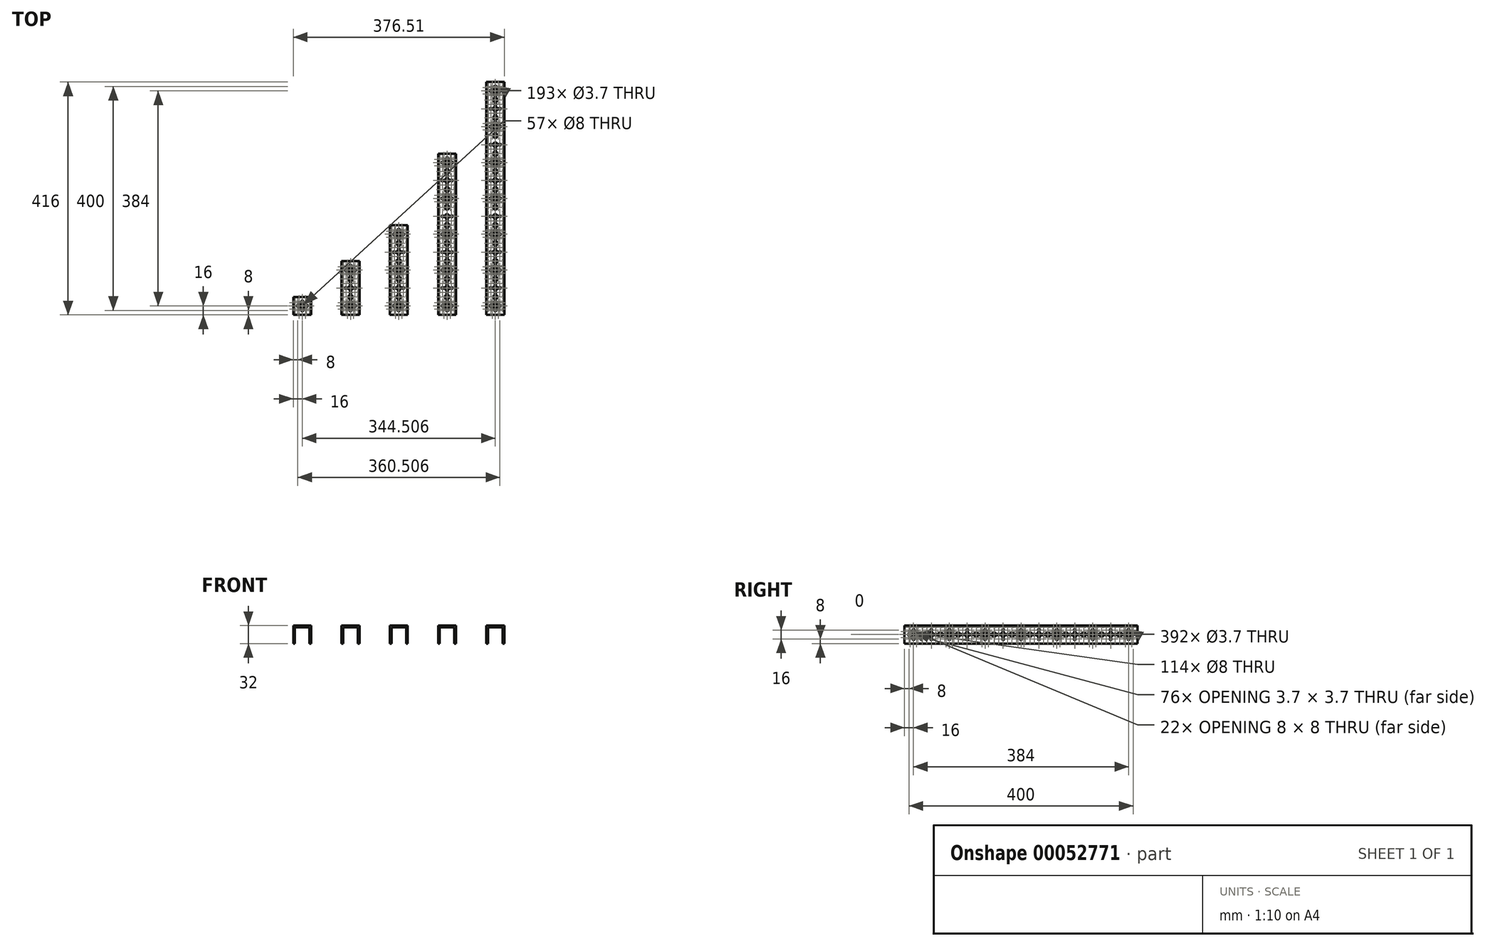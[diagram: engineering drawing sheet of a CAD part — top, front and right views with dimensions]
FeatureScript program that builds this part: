
annotation { "Feature Type Name" : "Feature", "Feature Type Description" : "" }
export const myFeature = defineFeature(function(context is Context, id is Id, definition is map)
    precondition{}
    {
        {
            var Q0;
            Q0=qCreatedBy(makeId("Front.planeOp"),FACE);
            var sketch = newSketch(context, id + "F0", { "sketchPlane" : qUnion([Q0])});
            skLineSegment(sketch, "E0", {"start": v(-16, 0) * mm, "end": v(16, 0) * mm});
            skLineSegment(sketch, "E1", {"start": v(16, 0) * mm, "end": v(16, -32) * mm});
            skLineSegment(sketch, "E2", {"start": v(-16, 0) * mm, "end": v(-16, -32) * mm});
            skLineSegment(sketch, "E3.0", {"start": v(-13, -3) * mm, "end": v(-13, -32) * mm});
            skLineSegment(sketch, "E3.1", {"start": v(-13, -3) * mm, "end": v(13, -3) * mm});
            skLineSegment(sketch, "E3.2", {"start": v(13, -3) * mm, "end": v(13, -32) * mm});
            skLineSegment(sketch, "E4", {"start": v(-16, -32) * mm, "end": v(-13, -32) * mm});
            skLineSegment(sketch, "E5", {"start": v(13, -32) * mm, "end": v(16, -32) * mm});
            skSolve(sketch);
        }
        {
            var Q0;
            Q0 = qSketchRegion(id + "F0", true);
            extrude(context, id + "F1", {"entities" : qUnion([Q0]), "oppositeDirection" : true, "depth" : 32 * mm});
        }
        {
            var Q0;
            Q0=makeQuery(id+"F1.opExtrude","SWEPT_FACE",FACE,{"disambiguationData":[OSD([sQuery(id+"F0.wireOp",EDGE,"E1")])]});
            var sketch = newSketch(context, id + "F2", { "sketchPlane" : qUnion([Q0])});
            skCircle(sketch, "E6", {"center": v(16, -16) * mm, "radius": 4 * mm});
            skCircle(sketch, "E7", {"center": v(10.34, -10.34) * mm, "radius": 1.85 * mm});
            skCircle(sketch, "E8", {"center": v(16, -8) * mm, "radius": 1.85 * mm});
            skCircle(sketch, "E9", {"center": v(21.66, -10.34) * mm, "radius": 1.85 * mm});
            skCircle(sketch, "E10", {"center": v(24, -16) * mm, "radius": 1.85 * mm});
            skCircle(sketch, "E11", {"center": v(21.66, -21.66) * mm, "radius": 1.85 * mm});
            skCircle(sketch, "E12", {"center": v(16, -24) * mm, "radius": 1.85 * mm});
            skCircle(sketch, "E13", {"center": v(8, -16) * mm, "radius": 1.85 * mm});
            skCircle(sketch, "E14", {"center": v(10.34, -21.66) * mm, "radius": 1.85 * mm});
            skCircle(sketch, "E15", {"center": v(16, -16) * mm, "radius": 8 * mm});
            skLineSegment(sketch, "E16", {"start": v(16, -8) * mm, "end": v(16, -24) * mm});
            skLineSegment(sketch, "E17", {"start": v(8, -16) * mm, "end": v(24, -16) * mm});
            skLineSegment(sketch, "E18", {"start": v(21.66, -10.34) * mm, "end": v(10.34, -21.66) * mm});
            skLineSegment(sketch, "E19", {"start": v(10.34, -10.34) * mm, "end": v(21.66, -21.66) * mm});
            skSolve(sketch);
        }
        {
            var Q0;
            Q0=makeQuery(id+"F1.opExtrude","SWEPT_FACE",FACE,{"disambiguationData":[OSD([sQuery(id+"F0.wireOp",EDGE,"E0")])]});
            var sketch = newSketch(context, id + "F3", { "sketchPlane" : qUnion([Q0])});
            skCircle(sketch, "E20", {"center": v(0, 16) * mm, "radius": 4 * mm});
            skCircle(sketch, "E21", {"center": v(-5.66, 21.66) * mm, "radius": 1.85 * mm});
            skCircle(sketch, "E22", {"center": v(0, 24) * mm, "radius": 1.85 * mm});
            skCircle(sketch, "E23", {"center": v(5.66, 21.66) * mm, "radius": 1.85 * mm});
            skCircle(sketch, "E24", {"center": v(8, 16) * mm, "radius": 1.85 * mm});
            skCircle(sketch, "E25", {"center": v(5.66, 10.34) * mm, "radius": 1.85 * mm});
            skCircle(sketch, "E26", {"center": v(0, 8) * mm, "radius": 1.85 * mm});
            skCircle(sketch, "E27", {"center": v(-8, 16) * mm, "radius": 1.85 * mm});
            skCircle(sketch, "E28", {"center": v(-5.66, 10.34) * mm, "radius": 1.85 * mm});
            skCircle(sketch, "E29", {"center": v(0, 16) * mm, "radius": 8 * mm});
            skLineSegment(sketch, "E30", {"start": v(0, 24) * mm, "end": v(0, 8) * mm});
            skLineSegment(sketch, "E31", {"start": v(-8, 16) * mm, "end": v(8, 16) * mm});
            skLineSegment(sketch, "E32", {"start": v(5.66, 21.66) * mm, "end": v(-5.66, 10.34) * mm});
            skLineSegment(sketch, "E33", {"start": v(-5.66, 21.66) * mm, "end": v(5.66, 10.34) * mm});
            skSolve(sketch);
        }
        {
            var Q0;
            Q0=sQuery(id+"F3.wireOp",VERTEX,"E21.center");
            var Q1;
            Q1=sQuery(id+"F3.wireOp",VERTEX,"E22.center");
            var Q2;
            Q2=sQuery(id+"F3.wireOp",VERTEX,"E23.center");
            var Q3;
            Q3=sQuery(id+"F3.wireOp",VERTEX,"E31.start");
            var Q4;
            Q4=sQuery(id+"F3.wireOp",VERTEX,"E24.center");
            var Q5;
            Q5=sQuery(id+"F3.wireOp",VERTEX,"E28.center");
            var Q6;
            Q6=sQuery(id+"F3.wireOp",VERTEX,"E30.end");
            var Q7;
            Q7=sQuery(id+"F3.wireOp",VERTEX,"E33.end");
            var Q8;
            Q8=sQuery(id+"F2.wireOp",VERTEX,"E16.start");
            var Q9;
            Q9=sQuery(id+"F2.wireOp",VERTEX,"E9.center");
            var Q10;
            Q10=sQuery(id+"F2.wireOp",VERTEX,"E10.center");
            var Q11;
            Q11=sQuery(id+"F2.wireOp",VERTEX,"E7.center");
            var Q12;
            Q12=sQuery(id+"F2.wireOp",VERTEX,"E17.start");
            var Q13;
            Q13=sQuery(id+"F2.wireOp",VERTEX,"E14.center");
            var Q14;
            Q14=sQuery(id+"F2.wireOp",VERTEX,"E16.end");
            var Q15;
            Q15=sQuery(id+"F2.wireOp",VERTEX,"E19.end");
            var Q16;
            Q16=makeQuery(id+"F1.opExtrude","SWEPT_BODY",BODY,{"disambiguationData":[OSD([sQuery(id+"F0.wireOp",EDGE,"E0"),sQuery(id+"F0.wireOp",EDGE,"E1"),sQuery(id+"F0.wireOp",EDGE,"E2"),sQuery(id+"F0.wireOp",EDGE,"E3.0"),sQuery(id+"F0.wireOp",EDGE,"E3.1"),sQuery(id+"F0.wireOp",EDGE,"E3.2"),sQuery(id+"F0.wireOp",EDGE,"E4"),sQuery(id+"F0.wireOp",EDGE,"E5")])]});
            hole(context, id + "F4", {"style" : HoleStyle.SIMPLE, "holeDiameter" : 3.7 * mm, "endStyle" : HoleEndStyle.THROUGH, "locations" : qUnion([Q0, Q1, Q2, Q3, Q4, Q5, Q6, Q7, Q8, Q9, Q10, Q11, Q12, Q13, Q14, Q15]), "scope" : qUnion([Q16])});
        }
        {
            var Q0;
            Q0=sQuery(id+"F3.wireOp",VERTEX,"E29.center");
            var Q1;
            Q1=sQuery(id+"F2.wireOp",VERTEX,"E6.center");
            var Q2;
            Q2=makeQuery(id+"F1.opExtrude","SWEPT_BODY",BODY,{"disambiguationData":[OSD([sQuery(id+"F0.wireOp",EDGE,"E0"),sQuery(id+"F0.wireOp",EDGE,"E1"),sQuery(id+"F0.wireOp",EDGE,"E2"),sQuery(id+"F0.wireOp",EDGE,"E3.0"),sQuery(id+"F0.wireOp",EDGE,"E3.1"),sQuery(id+"F0.wireOp",EDGE,"E3.2"),sQuery(id+"F0.wireOp",EDGE,"E4"),sQuery(id+"F0.wireOp",EDGE,"E5")])]});
            hole(context, id + "F5", {"style" : HoleStyle.SIMPLE, "holeDiameter" : 8 * mm, "endStyle" : HoleEndStyle.THROUGH, "locations" : qUnion([Q0, Q1]), "scope" : qUnion([Q2])});
        }
        {
            var Q0;
            Q0=makeQuery(id+"F1.opExtrude","SWEPT_BODY",BODY,{"disambiguationData":[OSD([sQuery(id+"F0.wireOp",EDGE,"E0"),sQuery(id+"F0.wireOp",EDGE,"E1"),sQuery(id+"F0.wireOp",EDGE,"E2"),sQuery(id+"F0.wireOp",EDGE,"E3.0"),sQuery(id+"F0.wireOp",EDGE,"E3.1"),sQuery(id+"F0.wireOp",EDGE,"E3.2"),sQuery(id+"F0.wireOp",EDGE,"E4"),sQuery(id+"F0.wireOp",EDGE,"E5")])]});
            transform(context, id + "F6", {"entities" : qUnion([Q0]), "transformType" : TransformType.TRANSLATION_3D, "dx" : 86.13 * mm, "dy" : 0 * mm, "dz" : 0 * mm, "makeCopy" : true});
        }
        {
            var Q0;
            Q0=makeQuery(id+"F6.opPattern","COPY",FACE,{"derivedFrom":makeQuery(id+"F1.opExtrude","CAP_FACE",FACE,{"disambiguationData":[OSD([sQuery(id+"F0.wireOp",EDGE,"E0"),sQuery(id+"F0.wireOp",EDGE,"E1"),sQuery(id+"F0.wireOp",EDGE,"E2"),sQuery(id+"F0.wireOp",EDGE,"E3.0"),sQuery(id+"F0.wireOp",EDGE,"E3.1"),sQuery(id+"F0.wireOp",EDGE,"E3.2"),sQuery(id+"F0.wireOp",EDGE,"E4"),sQuery(id+"F0.wireOp",EDGE,"E5")])],"isStart":false}),"instanceName":"1"});
            extrude(context, id + "F7", {"entities" : qUnion([Q0]), "operationType" : NewBodyOperationType.ADD, "depth" : 64 * mm});
        }
        {
            var Q0;
            {var subQ0=sQuery(id+"F0.wireOp",EDGE,"E1");Q0=makeQuery(id+"F7.boolean.opBoolean","MERGE",FACE,{"derivedFrom":[makeQuery(id+"F6.opPattern","COPY",FACE,{"derivedFrom":makeQuery(id+"F1.opExtrude","SWEPT_FACE",FACE,{"disambiguationData":[OSD([subQ0])]}),"instanceName":"1"}),makeQuery(id+"F7.opExtrude","SWEPT_FACE",FACE,{"disambiguationData":[OSD([subQ0])]})]});}
            var sketch = newSketch(context, id + "F8", { "sketchPlane" : qUnion([Q0])});
            skCircle(sketch, "E34", {"center": v(48, -24) * mm, "radius": 1.85 * mm});
            skLineSegment(sketch, "E35", {"start": v(48, -8) * mm, "end": v(48, -24) * mm});
            skLineSegment(sketch, "E36", {"start": v(40, -16) * mm, "end": v(56, -16) * mm});
            skCircle(sketch, "E37", {"center": v(48, -16) * mm, "radius": 8 * mm});
            skCircle(sketch, "E38", {"center": v(48, -16) * mm, "radius": 4 * mm});
            skCircle(sketch, "E39", {"center": v(48, -8) * mm, "radius": 1.85 * mm});
            skCircle(sketch, "E40", {"center": v(56, -16) * mm, "radius": 1.85 * mm});
            skCircle(sketch, "E41", {"center": v(40, -16) * mm, "radius": 1.85 * mm});
            skCircle(sketch, "E42.0", {"center": v(24, -16) * mm, "radius": 1.85 * mm});
            skCircle(sketch, "E43", {"center": v(80, -24) * mm, "radius": 1.85 * mm});
            skLineSegment(sketch, "E44", {"start": v(85.66, -10.34) * mm, "end": v(74.34, -21.66) * mm});
            skLineSegment(sketch, "E45", {"start": v(74.34, -10.34) * mm, "end": v(85.66, -21.66) * mm});
            skLineSegment(sketch, "E46", {"start": v(80, -8) * mm, "end": v(80, -24) * mm});
            skLineSegment(sketch, "E47", {"start": v(72, -16) * mm, "end": v(88, -16) * mm});
            skCircle(sketch, "E48", {"center": v(80, -16) * mm, "radius": 8 * mm});
            skCircle(sketch, "E49", {"center": v(74.34, -21.66) * mm, "radius": 1.85 * mm});
            skCircle(sketch, "E50", {"center": v(80, -16) * mm, "radius": 4 * mm});
            skCircle(sketch, "E51", {"center": v(74.34, -10.34) * mm, "radius": 1.85 * mm});
            skCircle(sketch, "E52", {"center": v(80, -8) * mm, "radius": 1.85 * mm});
            skCircle(sketch, "E53", {"center": v(85.66, -10.34) * mm, "radius": 1.85 * mm});
            skCircle(sketch, "E54", {"center": v(88, -16) * mm, "radius": 1.85 * mm});
            skCircle(sketch, "E55", {"center": v(85.66, -21.66) * mm, "radius": 1.85 * mm});
            skCircle(sketch, "E56", {"center": v(72, -16) * mm, "radius": 1.85 * mm});
            skCircle(sketch, "E57", {"center": v(32, -16) * mm, "radius": 4 * mm});
            skCircle(sketch, "E58", {"center": v(64, -16) * mm, "radius": 4 * mm});
            skSolve(sketch);
        }
        {
            var Q0;
            {var subQ0=sQuery(id+"F0.wireOp",EDGE,"E0");Q0=makeQuery(id+"F7.boolean.opBoolean","MERGE",FACE,{"derivedFrom":[makeQuery(id+"F6.opPattern","COPY",FACE,{"derivedFrom":makeQuery(id+"F1.opExtrude","SWEPT_FACE",FACE,{"disambiguationData":[OSD([subQ0])]}),"instanceName":"1"}),makeQuery(id+"F7.opExtrude","SWEPT_FACE",FACE,{"disambiguationData":[OSD([subQ0])]})]});}
            var sketch = newSketch(context, id + "F9", { "sketchPlane" : qUnion([Q0])});
            skCircle(sketch, "E59", {"center": v(86.13, 32) * mm, "radius": 4 * mm});
            skCircle(sketch, "E60.0", {"center": v(86.13, 24) * mm, "radius": 1.85 * mm});
            skCircle(sketch, "E61", {"center": v(86.13, 48) * mm, "radius": 4 * mm});
            skCircle(sketch, "E62", {"center": v(86.13, 40) * mm, "radius": 1.85 * mm});
            skLineSegment(sketch, "E63", {"start": v(86.13, 40) * mm, "end": v(86.13, 48) * mm});
            skCircle(sketch, "E64.1.0", {"center": v(78.13, 48) * mm, "radius": 1.85 * mm});
            skCircle(sketch, "E64.2.0", {"center": v(86.13, 56) * mm, "radius": 1.85 * mm});
            skCircle(sketch, "E64.3.0", {"center": v(94.13, 48) * mm, "radius": 1.85 * mm});
            skLineSegment(sketch, "E64.anchor1", {"start": v(86.13, 48) * mm, "end": v(86.13, 40) * mm, "construction": true});
            skLineSegment(sketch, "E64.anchor2", {"start": v(86.13, 48) * mm, "end": v(94.13, 48) * mm, "construction": true});
            skCircle(sketch, "E65", {"center": v(86.13, 64) * mm, "radius": 4 * mm});
            skCircle(sketch, "E66", {"center": v(86.13, 80) * mm, "radius": 4 * mm});
            skCircle(sketch, "E67", {"center": v(86.13, 72) * mm, "radius": 1.85 * mm});
            skLineSegment(sketch, "E68", {"start": v(86.13, 80) * mm, "end": v(86.13, 72) * mm});
            skCircle(sketch, "E69.1.0", {"center": v(91.78, 74.34) * mm, "radius": 1.85 * mm});
            skCircle(sketch, "E69.2.0", {"center": v(94.13, 80) * mm, "radius": 1.85 * mm});
            skCircle(sketch, "E69.3.0", {"center": v(91.78, 85.66) * mm, "radius": 1.85 * mm});
            skCircle(sketch, "E69.4.0", {"center": v(86.13, 88) * mm, "radius": 1.85 * mm});
            skCircle(sketch, "E69.5.0", {"center": v(80.47, 85.66) * mm, "radius": 1.85 * mm});
            skCircle(sketch, "E69.6.0", {"center": v(78.13, 80) * mm, "radius": 1.85 * mm});
            skCircle(sketch, "E69.7.0", {"center": v(80.47, 74.34) * mm, "radius": 1.85 * mm});
            skSolve(sketch);
        }
        {
            var Q0;
            Q0=sQuery(id+"F8.wireOp",VERTEX,"E39.center");
            var Q1;
            Q1=sQuery(id+"F8.wireOp",VERTEX,"E41.center");
            var Q2;
            Q2=sQuery(id+"F8.wireOp",VERTEX,"E40.center");
            var Q3;
            Q3=sQuery(id+"F8.wireOp",VERTEX,"E34.center");
            var Q4;
            Q4=sQuery(id+"F8.wireOp",VERTEX,"E51.center");
            var Q5;
            Q5=sQuery(id+"F8.wireOp",VERTEX,"E47.start");
            var Q6;
            Q6=sQuery(id+"F8.wireOp",VERTEX,"E44.end");
            var Q7;
            Q7=sQuery(id+"F8.wireOp",VERTEX,"E46.end");
            var Q8;
            Q8=sQuery(id+"F8.wireOp",VERTEX,"E47.end");
            var Q9;
            Q9=sQuery(id+"F8.wireOp",VERTEX,"E44.start");
            var Q10;
            Q10=sQuery(id+"F8.wireOp",VERTEX,"E52.center");
            var Q11;
            Q11=sQuery(id+"F8.wireOp",VERTEX,"E45.end");
            var Q12;
            Q12=sQuery(id+"F9.wireOp",VERTEX,"E64.3.0.center");
            var Q13;
            Q13=sQuery(id+"F9.wireOp",VERTEX,"E64.anchor1.end");
            var Q14;
            Q14=sQuery(id+"F9.wireOp",VERTEX,"E64.1.0.center");
            var Q15;
            Q15=sQuery(id+"F9.wireOp",VERTEX,"E64.2.0.center");
            var Q16;
            Q16=sQuery(id+"F9.wireOp",VERTEX,"E69.1.0.center");
            var Q17;
            Q17=sQuery(id+"F9.wireOp",VERTEX,"E68.end");
            var Q18;
            Q18=sQuery(id+"F9.wireOp",VERTEX,"E69.7.0.center");
            var Q19;
            Q19=sQuery(id+"F9.wireOp",VERTEX,"E69.6.0.center");
            var Q20;
            Q20=sQuery(id+"F9.wireOp",VERTEX,"E69.6.0.center");
            var Q21;
            Q21=sQuery(id+"F9.wireOp",VERTEX,"E69.5.0.center");
            var Q22;
            Q22=sQuery(id+"F9.wireOp",VERTEX,"E69.4.0.center");
            var Q23;
            Q23=sQuery(id+"F9.wireOp",VERTEX,"E69.3.0.center");
            var Q24;
            Q24=sQuery(id+"F9.wireOp",VERTEX,"E69.2.0.center");
            var Q25;
            Q25=makeQuery(id+"F6.opPattern","COPY",BODY,{"derivedFrom":makeQuery(id+"F1.opExtrude","SWEPT_BODY",BODY,{"disambiguationData":[OSD([sQuery(id+"F0.wireOp",EDGE,"E0"),sQuery(id+"F0.wireOp",EDGE,"E1"),sQuery(id+"F0.wireOp",EDGE,"E2"),sQuery(id+"F0.wireOp",EDGE,"E3.0"),sQuery(id+"F0.wireOp",EDGE,"E3.1"),sQuery(id+"F0.wireOp",EDGE,"E3.2"),sQuery(id+"F0.wireOp",EDGE,"E4"),sQuery(id+"F0.wireOp",EDGE,"E5")])]}),"instanceName":"1"});
            hole(context, id + "F10", {"style" : HoleStyle.SIMPLE, "holeDiameter" : 3.7 * mm, "endStyle" : HoleEndStyle.THROUGH, "locations" : qUnion([Q0, Q1, Q2, Q3, Q4, Q5, Q6, Q7, Q8, Q9, Q10, Q11, Q12, Q13, Q14, Q15, Q16, Q17, Q18, Q19, Q20, Q21, Q22, Q23, Q24]), "scope" : qUnion([Q25])});
        }
        {
            var Q0;
            Q0=sQuery(id+"F8.wireOp",VERTEX,"E37.center");
            var Q1;
            Q1=sQuery(id+"F8.wireOp",VERTEX,"E57.center");
            var Q2;
            Q2=sQuery(id+"F8.wireOp",VERTEX,"E58.center");
            var Q3;
            Q3=sQuery(id+"F8.wireOp",VERTEX,"E48.center");
            var Q4;
            Q4=sQuery(id+"F9.wireOp",VERTEX,"E59.center");
            var Q5;
            Q5=sQuery(id+"F9.wireOp",VERTEX,"E61.center");
            var Q6;
            Q6=sQuery(id+"F9.wireOp",VERTEX,"E65.center");
            var Q7;
            Q7=sQuery(id+"F9.wireOp",VERTEX,"E66.center");
            var Q8;
            Q8=makeQuery(id+"F6.opPattern","COPY",BODY,{"derivedFrom":makeQuery(id+"F1.opExtrude","SWEPT_BODY",BODY,{"disambiguationData":[OSD([sQuery(id+"F0.wireOp",EDGE,"E0"),sQuery(id+"F0.wireOp",EDGE,"E1"),sQuery(id+"F0.wireOp",EDGE,"E2"),sQuery(id+"F0.wireOp",EDGE,"E3.0"),sQuery(id+"F0.wireOp",EDGE,"E3.1"),sQuery(id+"F0.wireOp",EDGE,"E3.2"),sQuery(id+"F0.wireOp",EDGE,"E4"),sQuery(id+"F0.wireOp",EDGE,"E5")])]}),"instanceName":"1"});
            hole(context, id + "F11", {"style" : HoleStyle.SIMPLE, "holeDiameter" : 8 * mm, "endStyle" : HoleEndStyle.THROUGH, "locations" : qUnion([Q0, Q1, Q2, Q3, Q4, Q5, Q6, Q7]), "scope" : qUnion([Q8])});
        }
        {
            var Q0;
            Q0=makeQuery(id+"F6.opPattern","COPY",BODY,{"derivedFrom":makeQuery(id+"F1.opExtrude","SWEPT_BODY",BODY,{"disambiguationData":[OSD([sQuery(id+"F0.wireOp",EDGE,"E0"),sQuery(id+"F0.wireOp",EDGE,"E1"),sQuery(id+"F0.wireOp",EDGE,"E2"),sQuery(id+"F0.wireOp",EDGE,"E3.0"),sQuery(id+"F0.wireOp",EDGE,"E3.1"),sQuery(id+"F0.wireOp",EDGE,"E3.2"),sQuery(id+"F0.wireOp",EDGE,"E4"),sQuery(id+"F0.wireOp",EDGE,"E5")])]}),"instanceName":"1"});
            transform(context, id + "F12", {"entities" : qUnion([Q0]), "transformType" : TransformType.TRANSLATION_3D, "dx" : 86.13 * mm, "dy" : 0 * mm, "dz" : 0 * mm, "makeCopy" : true});
        }
        {
            var Q0;
            Q0=makeQuery(id+"F12.opPattern","COPY",FACE,{"derivedFrom":makeQuery(id+"F7.opExtrude","CAP_FACE",FACE,{"disambiguationData":[OSD([sQuery(id+"F0.wireOp",EDGE,"E0"),sQuery(id+"F0.wireOp",EDGE,"E1"),sQuery(id+"F0.wireOp",EDGE,"E2"),sQuery(id+"F0.wireOp",EDGE,"E3.0"),sQuery(id+"F0.wireOp",EDGE,"E3.1"),sQuery(id+"F0.wireOp",EDGE,"E3.2"),sQuery(id+"F0.wireOp",EDGE,"E4"),sQuery(id+"F0.wireOp",EDGE,"E5")])],"isStart":false}),"instanceName":"1"});
            extrude(context, id + "F13", {"entities" : qUnion([Q0]), "operationType" : NewBodyOperationType.ADD, "depth" : 64 * mm});
        }
        {
            var Q0;
            {var subQ0=sQuery(id+"F0.wireOp",EDGE,"E1");Q0=makeQuery(id+"F13.boolean.opBoolean","MERGE",FACE,{"derivedFrom":[makeQuery(id+"F12.opPattern","COPY",FACE,{"derivedFrom":makeQuery(id+"F7.boolean.opBoolean","MERGE",FACE,{"derivedFrom":[makeQuery(id+"F6.opPattern","COPY",FACE,{"derivedFrom":makeQuery(id+"F1.opExtrude","SWEPT_FACE",FACE,{"disambiguationData":[OSD([subQ0])]}),"instanceName":"1"}),makeQuery(id+"F7.opExtrude","SWEPT_FACE",FACE,{"disambiguationData":[OSD([subQ0])]})]}),"instanceName":"1"}),makeQuery(id+"F13.opExtrude","SWEPT_FACE",FACE,{"disambiguationData":[OSD([subQ0])]})]});}
            var sketch = newSketch(context, id + "F14", { "sketchPlane" : qUnion([Q0])});
            skCircle(sketch, "E70", {"center": v(112, -16) * mm, "radius": 8 * mm});
            skCircle(sketch, "E71", {"center": v(128, -16) * mm, "radius": 4 * mm});
            skCircle(sketch, "E72", {"center": v(96, -16) * mm, "radius": 4 * mm});
            skCircle(sketch, "E73.0", {"center": v(88, -16) * mm, "radius": 1.85 * mm});
            skCircle(sketch, "E74", {"center": v(138.34, -10.34) * mm, "radius": 1.85 * mm});
            skCircle(sketch, "E75", {"center": v(144, -16) * mm, "radius": 4 * mm});
            skCircle(sketch, "E76", {"center": v(149.66, -10.34) * mm, "radius": 1.85 * mm});
            skCircle(sketch, "E77", {"center": v(144, -8) * mm, "radius": 1.85 * mm});
            skCircle(sketch, "E78", {"center": v(149.66, -21.66) * mm, "radius": 1.85 * mm});
            skCircle(sketch, "E79", {"center": v(152, -16) * mm, "radius": 1.85 * mm});
            skCircle(sketch, "E80", {"center": v(138.34, -21.66) * mm, "radius": 1.85 * mm});
            skCircle(sketch, "E81", {"center": v(144, -16) * mm, "radius": 8 * mm});
            skCircle(sketch, "E82", {"center": v(112, -24) * mm, "radius": 1.85 * mm});
            skLineSegment(sketch, "E83", {"start": v(104, -16) * mm, "end": v(120, -16) * mm});
            skLineSegment(sketch, "E84", {"start": v(112, -8) * mm, "end": v(112, -24) * mm});
            skCircle(sketch, "E85", {"center": v(112, -16) * mm, "radius": 4 * mm});
            skLineSegment(sketch, "E86", {"start": v(136, -16) * mm, "end": v(152, -16) * mm});
            skLineSegment(sketch, "E87", {"start": v(144, -8) * mm, "end": v(144, -24) * mm});
            skLineSegment(sketch, "E88", {"start": v(138.34, -10.34) * mm, "end": v(149.66, -21.66) * mm});
            skCircle(sketch, "E89", {"center": v(120, -16) * mm, "radius": 1.85 * mm});
            skCircle(sketch, "E90", {"center": v(112, -8) * mm, "radius": 1.85 * mm});
            skCircle(sketch, "E91", {"center": v(104, -16) * mm, "radius": 1.85 * mm});
            skLineSegment(sketch, "E92", {"start": v(149.66, -10.34) * mm, "end": v(138.34, -21.66) * mm});
            skCircle(sketch, "E93", {"center": v(144, -24) * mm, "radius": 1.85 * mm});
            skCircle(sketch, "E94", {"center": v(136, -16) * mm, "radius": 1.85 * mm});
            skLineSegment(sketch, "E95", {"start": v(88, -16) * mm, "end": v(152, -16) * mm});
            skSolve(sketch);
        }
        {
            var Q0;
            {var subQ0=sQuery(id+"F0.wireOp",EDGE,"E0");Q0=makeQuery(id+"F13.boolean.opBoolean","MERGE",FACE,{"derivedFrom":[makeQuery(id+"F12.opPattern","COPY",FACE,{"derivedFrom":makeQuery(id+"F7.boolean.opBoolean","MERGE",FACE,{"derivedFrom":[makeQuery(id+"F6.opPattern","COPY",FACE,{"derivedFrom":makeQuery(id+"F1.opExtrude","SWEPT_FACE",FACE,{"disambiguationData":[OSD([subQ0])]}),"instanceName":"1"}),makeQuery(id+"F7.opExtrude","SWEPT_FACE",FACE,{"disambiguationData":[OSD([subQ0])]})]}),"instanceName":"1"}),makeQuery(id+"F13.opExtrude","SWEPT_FACE",FACE,{"disambiguationData":[OSD([subQ0])]})]});}
            var sketch = newSketch(context, id + "F15", { "sketchPlane" : qUnion([Q0])});
            skPoint(sketch, "E96.center", {"position": v(172.25, 144) * mm});
            skPoint(sketch, "E97.center", {"position": v(172.25, 112) * mm});
            skCircle(sketch, "E96.5.0", {"center": v(166.6, 149.66) * mm, "radius": 1.85 * mm});
            skCircle(sketch, "E96.4.0", {"center": v(172.25, 152) * mm, "radius": 1.85 * mm});
            skCircle(sketch, "E96.6.0", {"center": v(164.25, 144) * mm, "radius": 1.85 * mm});
            skCircle(sketch, "E96.2.0", {"center": v(180.25, 144) * mm, "radius": 1.85 * mm});
            skCircle(sketch, "E98.0", {"center": v(172.25, 88) * mm, "radius": 1.85 * mm});
            skCircle(sketch, "E99", {"center": v(172.25, 96) * mm, "radius": 4 * mm});
            skCircle(sketch, "E97.1.0", {"center": v(164.25, 112) * mm, "radius": 1.85 * mm});
            skCircle(sketch, "E100", {"center": v(172.25, 128) * mm, "radius": 4 * mm});
            skCircle(sketch, "E96.3.0", {"center": v(177.9, 149.66) * mm, "radius": 1.85 * mm});
            skCircle(sketch, "E96.7.0", {"center": v(166.6, 138.34) * mm, "radius": 1.85 * mm});
            skCircle(sketch, "E96.1.0", {"center": v(177.9, 138.34) * mm, "radius": 1.85 * mm});
            skCircle(sketch, "E101", {"center": v(172.25, 136) * mm, "radius": 1.85 * mm});
            skCircle(sketch, "E97.2.0", {"center": v(172.25, 120) * mm, "radius": 1.85 * mm});
            skCircle(sketch, "E97.3.0", {"center": v(180.25, 112) * mm, "radius": 1.85 * mm});
            skLineSegment(sketch, "E102", {"start": v(172.25, 144) * mm, "end": v(172.25, 136) * mm});
            skCircle(sketch, "E103", {"center": v(172.25, 104) * mm, "radius": 1.85 * mm});
            skCircle(sketch, "E104", {"center": v(172.25, 144) * mm, "radius": 4 * mm});
            skLineSegment(sketch, "E105", {"start": v(172.25, 104) * mm, "end": v(172.25, 112) * mm});
            skLineSegment(sketch, "E97.anchor2", {"start": v(172.25, 112) * mm, "end": v(180.25, 112) * mm, "construction": true});
            skLineSegment(sketch, "E97.anchor1", {"start": v(172.25, 112) * mm, "end": v(172.25, 104) * mm, "construction": true});
            skCircle(sketch, "E106", {"center": v(172.25, 112) * mm, "radius": 4 * mm});
            skSolve(sketch);
        }
        {
            var Q0;
            Q0=sQuery(id+"F15.wireOp",VERTEX,"E99.center");
            var Q1;
            Q1=sQuery(id+"F15.wireOp",VERTEX,"E97.center");
            var Q2;
            Q2=sQuery(id+"F15.wireOp",VERTEX,"E100.center");
            var Q3;
            Q3=sQuery(id+"F15.wireOp",VERTEX,"E96.center");
            var Q4;
            Q4=sQuery(id+"F14.wireOp",VERTEX,"E72.center");
            var Q5;
            Q5=sQuery(id+"F14.wireOp",VERTEX,"E70.center");
            var Q6;
            Q6=sQuery(id+"F14.wireOp",VERTEX,"E71.center");
            var Q7;
            Q7=sQuery(id+"F14.wireOp",VERTEX,"E75.center");
            var Q8;
            Q8=makeQuery(id+"F12.opPattern","COPY",BODY,{"derivedFrom":makeQuery(id+"F6.opPattern","COPY",BODY,{"derivedFrom":makeQuery(id+"F1.opExtrude","SWEPT_BODY",BODY,{"disambiguationData":[OSD([sQuery(id+"F0.wireOp",EDGE,"E0"),sQuery(id+"F0.wireOp",EDGE,"E1"),sQuery(id+"F0.wireOp",EDGE,"E2"),sQuery(id+"F0.wireOp",EDGE,"E3.0"),sQuery(id+"F0.wireOp",EDGE,"E3.1"),sQuery(id+"F0.wireOp",EDGE,"E3.2"),sQuery(id+"F0.wireOp",EDGE,"E4"),sQuery(id+"F0.wireOp",EDGE,"E5")])]}),"instanceName":"1"}),"instanceName":"1"});
            hole(context, id + "F16", {"style" : HoleStyle.SIMPLE, "holeDiameter" : 8 * mm, "endStyle" : HoleEndStyle.THROUGH, "locations" : qUnion([Q0, Q1, Q2, Q3, Q4, Q5, Q6, Q7]), "scope" : qUnion([Q8])});
        }
        {
            var Q0;
            Q0=sQuery(id+"F15.wireOp",VERTEX,"E103.center");
            var Q1;
            Q1=sQuery(id+"F15.wireOp",VERTEX,"E97.1.0.center");
            var Q2;
            Q2=sQuery(id+"F15.wireOp",VERTEX,"E97.2.0.center");
            var Q3;
            Q3=sQuery(id+"F15.wireOp",VERTEX,"E97.anchor2.end");
            var Q4;
            Q4=sQuery(id+"F14.wireOp",VERTEX,"E84.start");
            var Q5;
            Q5=sQuery(id+"F14.wireOp",VERTEX,"E84.end");
            var Q6;
            Q6=sQuery(id+"F14.wireOp",VERTEX,"E91.center");
            var Q7;
            Q7=sQuery(id+"F14.wireOp",VERTEX,"E83.end");
            var Q8;
            Q8=sQuery(id+"F15.wireOp",VERTEX,"E101.center");
            var Q9;
            Q9=sQuery(id+"F15.wireOp",VERTEX,"E96.1.0.center");
            var Q10;
            Q10=sQuery(id+"F15.wireOp",VERTEX,"E96.7.0.center");
            var Q11;
            Q11=sQuery(id+"F15.wireOp",VERTEX,"E96.6.0.center");
            var Q12;
            Q12=sQuery(id+"F15.wireOp",VERTEX,"E96.5.0.center");
            var Q13;
            Q13=sQuery(id+"F15.wireOp",VERTEX,"E96.4.0.center");
            var Q14;
            Q14=sQuery(id+"F15.wireOp",VERTEX,"E96.3.0.center");
            var Q15;
            Q15=sQuery(id+"F15.wireOp",VERTEX,"E96.2.0.center");
            var Q16;
            Q16=sQuery(id+"F14.wireOp",VERTEX,"E87.start");
            var Q17;
            Q17=sQuery(id+"F14.wireOp",VERTEX,"E88.start");
            var Q18;
            Q18=sQuery(id+"F14.wireOp",VERTEX,"E86.start");
            var Q19;
            Q19=sQuery(id+"F14.wireOp",VERTEX,"E92.end");
            var Q20;
            Q20=sQuery(id+"F14.wireOp",VERTEX,"E88.start");
            var Q21;
            Q21=sQuery(id+"F14.wireOp",VERTEX,"E87.end");
            var Q22;
            Q22=sQuery(id+"F14.wireOp",VERTEX,"E88.end");
            var Q23;
            Q23=sQuery(id+"F14.wireOp",VERTEX,"E86.end");
            var Q24;
            Q24=sQuery(id+"F14.wireOp",VERTEX,"E76.center");
            var Q25;
            Q25=makeQuery(id+"F12.opPattern","COPY",BODY,{"derivedFrom":makeQuery(id+"F6.opPattern","COPY",BODY,{"derivedFrom":makeQuery(id+"F1.opExtrude","SWEPT_BODY",BODY,{"disambiguationData":[OSD([sQuery(id+"F0.wireOp",EDGE,"E0"),sQuery(id+"F0.wireOp",EDGE,"E1"),sQuery(id+"F0.wireOp",EDGE,"E2"),sQuery(id+"F0.wireOp",EDGE,"E3.0"),sQuery(id+"F0.wireOp",EDGE,"E3.1"),sQuery(id+"F0.wireOp",EDGE,"E3.2"),sQuery(id+"F0.wireOp",EDGE,"E4"),sQuery(id+"F0.wireOp",EDGE,"E5")])]}),"instanceName":"1"}),"instanceName":"1"});
            hole(context, id + "F17", {"style" : HoleStyle.SIMPLE, "holeDiameter" : 3.7 * mm, "endStyle" : HoleEndStyle.THROUGH, "locations" : qUnion([Q0, Q1, Q2, Q3, Q4, Q5, Q6, Q7, Q8, Q9, Q10, Q11, Q12, Q13, Q14, Q15, Q16, Q17, Q18, Q19, Q20, Q21, Q22, Q23, Q24]), "scope" : qUnion([Q25])});
        }
        {
            var Q0;
            Q0=makeQuery(id+"F12.opPattern","COPY",BODY,{"derivedFrom":makeQuery(id+"F6.opPattern","COPY",BODY,{"derivedFrom":makeQuery(id+"F1.opExtrude","SWEPT_BODY",BODY,{"disambiguationData":[OSD([sQuery(id+"F0.wireOp",EDGE,"E0"),sQuery(id+"F0.wireOp",EDGE,"E1"),sQuery(id+"F0.wireOp",EDGE,"E2"),sQuery(id+"F0.wireOp",EDGE,"E3.0"),sQuery(id+"F0.wireOp",EDGE,"E3.1"),sQuery(id+"F0.wireOp",EDGE,"E3.2"),sQuery(id+"F0.wireOp",EDGE,"E4"),sQuery(id+"F0.wireOp",EDGE,"E5")])]}),"instanceName":"1"}),"instanceName":"1"});
            transform(context, id + "F18", {"entities" : qUnion([Q0]), "transformType" : TransformType.TRANSLATION_3D, "dx" : 86.13 * mm, "dy" : 0 * mm, "dz" : 0 * mm, "makeCopy" : true});
        }
        {
            var Q0;
            Q0=makeQuery(id+"F18.opPattern","COPY",FACE,{"derivedFrom":makeQuery(id+"F13.opExtrude","CAP_FACE",FACE,{"disambiguationData":[OSD([sQuery(id+"F0.wireOp",EDGE,"E0"),sQuery(id+"F0.wireOp",EDGE,"E1"),sQuery(id+"F0.wireOp",EDGE,"E2"),sQuery(id+"F0.wireOp",EDGE,"E3.0"),sQuery(id+"F0.wireOp",EDGE,"E3.1"),sQuery(id+"F0.wireOp",EDGE,"E3.2"),sQuery(id+"F0.wireOp",EDGE,"E4"),sQuery(id+"F0.wireOp",EDGE,"E5")])],"isStart":false}),"instanceName":"1"});
            extrude(context, id + "F19", {"entities" : qUnion([Q0]), "operationType" : NewBodyOperationType.ADD, "depth" : 128 * mm});
        }
        {
            var Q0;
            {var subQ0=sQuery(id+"F0.wireOp",EDGE,"E1");Q0=makeQuery(id+"F19.boolean.opBoolean","MERGE",FACE,{"derivedFrom":[makeQuery(id+"F18.opPattern","COPY",FACE,{"derivedFrom":makeQuery(id+"F13.boolean.opBoolean","MERGE",FACE,{"derivedFrom":[makeQuery(id+"F12.opPattern","COPY",FACE,{"derivedFrom":makeQuery(id+"F7.boolean.opBoolean","MERGE",FACE,{"derivedFrom":[makeQuery(id+"F6.opPattern","COPY",FACE,{"derivedFrom":makeQuery(id+"F1.opExtrude","SWEPT_FACE",FACE,{"disambiguationData":[OSD([subQ0])]}),"instanceName":"1"}),makeQuery(id+"F7.opExtrude","SWEPT_FACE",FACE,{"disambiguationData":[OSD([subQ0])]})]}),"instanceName":"1"}),makeQuery(id+"F13.opExtrude","SWEPT_FACE",FACE,{"disambiguationData":[OSD([subQ0])]})]}),"instanceName":"1"}),makeQuery(id+"F19.opExtrude","SWEPT_FACE",FACE,{"disambiguationData":[OSD([subQ0])]})]});}
            var sketch = newSketch(context, id + "F20", { "sketchPlane" : qUnion([Q0])});
            skLineSegment(sketch, "E107", {"start": v(144, -16) * mm, "end": v(288, -16) * mm, "construction": true});
            skCircle(sketch, "E108", {"center": v(160, -16) * mm, "radius": 4 * mm});
            skCircle(sketch, "E109", {"center": v(168, -16) * mm, "radius": 1.85 * mm});
            skCircle(sketch, "E110", {"center": v(176, -16) * mm, "radius": 4 * mm});
            skCircle(sketch, "E111.0", {"center": v(152, -16) * mm, "radius": 1.85 * mm});
            skCircle(sketch, "E112.1.0", {"center": v(176, -24) * mm, "radius": 1.85 * mm});
            skCircle(sketch, "E112.2.0", {"center": v(184, -16) * mm, "radius": 1.85 * mm});
            skCircle(sketch, "E112.3.0", {"center": v(176, -8) * mm, "radius": 1.85 * mm});
            skCircle(sketch, "E113", {"center": v(192, -16) * mm, "radius": 4 * mm});
            skCircle(sketch, "E114", {"center": v(200, -16) * mm, "radius": 1.85 * mm});
            skCircle(sketch, "E115", {"center": v(208, -16) * mm, "radius": 4 * mm});
            skCircle(sketch, "E116.1.0", {"center": v(202.34, -21.66) * mm, "radius": 1.85 * mm});
            skCircle(sketch, "E116.2.0", {"center": v(208, -24) * mm, "radius": 1.85 * mm});
            skCircle(sketch, "E116.3.0", {"center": v(213.66, -21.66) * mm, "radius": 1.85 * mm});
            skCircle(sketch, "E116.4.0", {"center": v(216, -16) * mm, "radius": 1.85 * mm});
            skCircle(sketch, "E116.5.0", {"center": v(213.66, -10.34) * mm, "radius": 1.85 * mm});
            skCircle(sketch, "E116.6.0", {"center": v(208, -8) * mm, "radius": 1.85 * mm});
            skCircle(sketch, "E116.7.0", {"center": v(202.34, -10.34) * mm, "radius": 1.85 * mm});
            skCircle(sketch, "E117", {"center": v(224, -16) * mm, "radius": 4 * mm});
            skCircle(sketch, "E118", {"center": v(232, -16) * mm, "radius": 1.85 * mm});
            skCircle(sketch, "E119", {"center": v(240, -16) * mm, "radius": 4 * mm});
            skCircle(sketch, "E120.1.0", {"center": v(240, -24) * mm, "radius": 1.85 * mm});
            skCircle(sketch, "E120.2.0", {"center": v(248, -16) * mm, "radius": 1.85 * mm});
            skCircle(sketch, "E120.3.0", {"center": v(240, -8) * mm, "radius": 1.85 * mm});
            skCircle(sketch, "E121", {"center": v(256, -16) * mm, "radius": 4 * mm});
            skCircle(sketch, "E122", {"center": v(264, -16) * mm, "radius": 1.85 * mm});
            skCircle(sketch, "E123", {"center": v(272, -16) * mm, "radius": 4 * mm});
            skCircle(sketch, "E124.1.0", {"center": v(266.34, -21.66) * mm, "radius": 1.85 * mm});
            skCircle(sketch, "E124.2.0", {"center": v(272, -24) * mm, "radius": 1.85 * mm});
            skCircle(sketch, "E124.3.0", {"center": v(277.66, -21.66) * mm, "radius": 1.85 * mm});
            skCircle(sketch, "E124.4.0", {"center": v(280, -16) * mm, "radius": 1.85 * mm});
            skCircle(sketch, "E124.5.0", {"center": v(277.66, -10.34) * mm, "radius": 1.85 * mm});
            skCircle(sketch, "E124.6.0", {"center": v(272, -8) * mm, "radius": 1.85 * mm});
            skCircle(sketch, "E124.7.0", {"center": v(266.34, -10.34) * mm, "radius": 1.85 * mm});
            skSolve(sketch);
        }
        {
            var Q0;
            {var subQ0=sQuery(id+"F0.wireOp",EDGE,"E0");Q0=makeQuery(id+"F19.boolean.opBoolean","MERGE",FACE,{"derivedFrom":[makeQuery(id+"F18.opPattern","COPY",FACE,{"derivedFrom":makeQuery(id+"F13.boolean.opBoolean","MERGE",FACE,{"derivedFrom":[makeQuery(id+"F12.opPattern","COPY",FACE,{"derivedFrom":makeQuery(id+"F7.boolean.opBoolean","MERGE",FACE,{"derivedFrom":[makeQuery(id+"F6.opPattern","COPY",FACE,{"derivedFrom":makeQuery(id+"F1.opExtrude","SWEPT_FACE",FACE,{"disambiguationData":[OSD([subQ0])]}),"instanceName":"1"}),makeQuery(id+"F7.opExtrude","SWEPT_FACE",FACE,{"disambiguationData":[OSD([subQ0])]})]}),"instanceName":"1"}),makeQuery(id+"F13.opExtrude","SWEPT_FACE",FACE,{"disambiguationData":[OSD([subQ0])]})]}),"instanceName":"1"}),makeQuery(id+"F19.opExtrude","SWEPT_FACE",FACE,{"disambiguationData":[OSD([subQ0])]})]});}
            var sketch = newSketch(context, id + "F21", { "sketchPlane" : qUnion([Q0])});
            skLineSegment(sketch, "E125", {"start": v(258.38, 152) * mm, "end": v(258.38, 288) * mm});
            skCircle(sketch, "E126", {"center": v(258.38, 160) * mm, "radius": 4 * mm});
            skCircle(sketch, "E127", {"center": v(258.38, 168) * mm, "radius": 1.85 * mm});
            skCircle(sketch, "E128", {"center": v(258.38, 176) * mm, "radius": 4 * mm});
            skCircle(sketch, "E129", {"center": v(258.38, 184) * mm, "radius": 1.85 * mm});
            skCircle(sketch, "E130", {"center": v(258.38, 192) * mm, "radius": 4 * mm});
            skCircle(sketch, "E131", {"center": v(258.38, 200) * mm, "radius": 1.85 * mm});
            skCircle(sketch, "E132.1.0", {"center": v(266.38, 176) * mm, "radius": 1.85 * mm});
            skCircle(sketch, "E132.3.0", {"center": v(250.38, 176) * mm, "radius": 1.85 * mm});
            skCircle(sketch, "E133", {"center": v(258.38, 208) * mm, "radius": 4 * mm});
            skCircle(sketch, "E134.1.0", {"center": v(264.04, 202.34) * mm, "radius": 1.85 * mm});
            skCircle(sketch, "E134.2.0", {"center": v(266.38, 208) * mm, "radius": 1.85 * mm});
            skCircle(sketch, "E134.3.0", {"center": v(264.04, 213.66) * mm, "radius": 1.85 * mm});
            skCircle(sketch, "E134.4.0", {"center": v(258.38, 216) * mm, "radius": 1.85 * mm});
            skCircle(sketch, "E134.5.0", {"center": v(252.72, 213.66) * mm, "radius": 1.85 * mm});
            skCircle(sketch, "E134.6.0", {"center": v(250.38, 208) * mm, "radius": 1.85 * mm});
            skCircle(sketch, "E134.7.0", {"center": v(252.72, 202.34) * mm, "radius": 1.85 * mm});
            skCircle(sketch, "E135", {"center": v(258.38, 224) * mm, "radius": 4 * mm});
            skCircle(sketch, "E136", {"center": v(258.38, 232) * mm, "radius": 1.85 * mm});
            skCircle(sketch, "E137", {"center": v(258.38, 240) * mm, "radius": 4 * mm});
            skCircle(sketch, "E138.1.0", {"center": v(266.38, 240) * mm, "radius": 1.85 * mm});
            skCircle(sketch, "E138.2.0", {"center": v(258.38, 248) * mm, "radius": 1.85 * mm});
            skCircle(sketch, "E138.3.0", {"center": v(250.38, 240) * mm, "radius": 1.85 * mm});
            skCircle(sketch, "E139", {"center": v(258.38, 256) * mm, "radius": 4 * mm});
            skCircle(sketch, "E140", {"center": v(258.38, 264) * mm, "radius": 1.85 * mm});
            skCircle(sketch, "E141", {"center": v(258.38, 272) * mm, "radius": 4 * mm});
            skCircle(sketch, "E142.1.0", {"center": v(264.04, 266.34) * mm, "radius": 1.85 * mm});
            skCircle(sketch, "E142.2.0", {"center": v(266.38, 272) * mm, "radius": 1.85 * mm});
            skCircle(sketch, "E142.3.0", {"center": v(264.04, 277.66) * mm, "radius": 1.85 * mm});
            skCircle(sketch, "E142.4.0", {"center": v(258.38, 280) * mm, "radius": 1.85 * mm});
            skCircle(sketch, "E142.5.0", {"center": v(252.72, 277.66) * mm, "radius": 1.85 * mm});
            skCircle(sketch, "E142.6.0", {"center": v(250.38, 272) * mm, "radius": 1.85 * mm});
            skCircle(sketch, "E142.7.0", {"center": v(252.72, 266.34) * mm, "radius": 1.85 * mm});
            skSolve(sketch);
        }
        {
            var Q0;
            Q0=sQuery(id+"F21.wireOp",VERTEX,"E126.center");
            var Q1;
            Q1=sQuery(id+"F21.wireOp",VERTEX,"E130.center");
            var Q2;
            Q2=sQuery(id+"F21.wireOp",VERTEX,"E133.center");
            var Q3;
            Q3=sQuery(id+"F21.wireOp",VERTEX,"E135.center");
            var Q4;
            Q4=sQuery(id+"F21.wireOp",VERTEX,"E137.center");
            var Q5;
            Q5=sQuery(id+"F21.wireOp",VERTEX,"E139.center");
            var Q6;
            Q6=sQuery(id+"F21.wireOp",VERTEX,"E141.center");
            var Q7;
            Q7=sQuery(id+"F20.wireOp",VERTEX,"E108.center");
            var Q8;
            Q8=sQuery(id+"F20.wireOp",VERTEX,"E110.center");
            var Q9;
            Q9=sQuery(id+"F20.wireOp",VERTEX,"E113.center");
            var Q10;
            Q10=sQuery(id+"F20.wireOp",VERTEX,"E115.center");
            var Q11;
            Q11=sQuery(id+"F20.wireOp",VERTEX,"E117.center");
            var Q12;
            Q12=sQuery(id+"F20.wireOp",VERTEX,"E119.center");
            var Q13;
            Q13=sQuery(id+"F20.wireOp",VERTEX,"E121.center");
            var Q14;
            Q14=sQuery(id+"F20.wireOp",VERTEX,"E123.center");
            var Q15;
            Q15=sQuery(id+"F21.wireOp",VERTEX,"E128.center");
            var Q16;
            Q16=makeQuery(id+"F18.opPattern","COPY",BODY,{"derivedFrom":makeQuery(id+"F12.opPattern","COPY",BODY,{"derivedFrom":makeQuery(id+"F6.opPattern","COPY",BODY,{"derivedFrom":makeQuery(id+"F1.opExtrude","SWEPT_BODY",BODY,{"disambiguationData":[OSD([sQuery(id+"F0.wireOp",EDGE,"E0"),sQuery(id+"F0.wireOp",EDGE,"E1"),sQuery(id+"F0.wireOp",EDGE,"E2"),sQuery(id+"F0.wireOp",EDGE,"E3.0"),sQuery(id+"F0.wireOp",EDGE,"E3.1"),sQuery(id+"F0.wireOp",EDGE,"E3.2"),sQuery(id+"F0.wireOp",EDGE,"E4"),sQuery(id+"F0.wireOp",EDGE,"E5")])]}),"instanceName":"1"}),"instanceName":"1"}),"instanceName":"1"});
            hole(context, id + "F22", {"style" : HoleStyle.SIMPLE, "holeDiameter" : 8 * mm, "endStyle" : HoleEndStyle.THROUGH, "locations" : qUnion([Q0, Q1, Q2, Q3, Q4, Q5, Q6, Q7, Q8, Q9, Q10, Q11, Q12, Q13, Q14, Q15]), "scope" : qUnion([Q16])});
        }
        {
            var Q0;
            Q0=sQuery(id+"F21.wireOp",VERTEX,"E127.center");
            var Q1;
            Q1=sQuery(id+"F21.wireOp",VERTEX,"E132.3.0.center");
            var Q2;
            Q2=sQuery(id+"F21.wireOp",VERTEX,"E132.1.0.center");
            var Q3;
            Q3=sQuery(id+"F21.wireOp",VERTEX,"E131.center");
            var Q4;
            Q4=sQuery(id+"F21.wireOp",VERTEX,"E134.7.0.center");
            var Q5;
            Q5=sQuery(id+"F21.wireOp",VERTEX,"E134.6.0.center");
            var Q6;
            Q6=sQuery(id+"F21.wireOp",VERTEX,"E134.5.0.center");
            var Q7;
            Q7=sQuery(id+"F21.wireOp",VERTEX,"E134.4.0.center");
            var Q8;
            Q8=sQuery(id+"F21.wireOp",VERTEX,"E134.3.0.center");
            var Q9;
            Q9=sQuery(id+"F21.wireOp",VERTEX,"E134.2.0.center");
            var Q10;
            Q10=sQuery(id+"F21.wireOp",VERTEX,"E134.1.0.center");
            var Q11;
            Q11=sQuery(id+"F21.wireOp",VERTEX,"E136.center");
            var Q12;
            Q12=sQuery(id+"F21.wireOp",VERTEX,"E138.3.0.center");
            var Q13;
            Q13=sQuery(id+"F21.wireOp",VERTEX,"E138.2.0.center");
            var Q14;
            Q14=sQuery(id+"F21.wireOp",VERTEX,"E138.1.0.center");
            var Q15;
            Q15=sQuery(id+"F21.wireOp",VERTEX,"E140.center");
            var Q16;
            Q16=sQuery(id+"F21.wireOp",VERTEX,"E142.7.0.center");
            var Q17;
            Q17=sQuery(id+"F21.wireOp",VERTEX,"E142.6.0.center");
            var Q18;
            Q18=sQuery(id+"F21.wireOp",VERTEX,"E142.5.0.center");
            var Q19;
            Q19=sQuery(id+"F21.wireOp",VERTEX,"E142.4.0.center");
            var Q20;
            Q20=sQuery(id+"F21.wireOp",VERTEX,"E142.3.0.center");
            var Q21;
            Q21=sQuery(id+"F21.wireOp",VERTEX,"E142.2.0.center");
            var Q22;
            Q22=sQuery(id+"F21.wireOp",VERTEX,"E142.1.0.center");
            var Q23;
            Q23=sQuery(id+"F20.wireOp",VERTEX,"E112.3.0.center");
            var Q24;
            Q24=sQuery(id+"F20.wireOp",VERTEX,"E109.center");
            var Q25;
            Q25=sQuery(id+"F21.wireOp",VERTEX,"E129.center");
            var Q26;
            Q26=sQuery(id+"F20.wireOp",VERTEX,"E112.1.0.center");
            var Q27;
            Q27=sQuery(id+"F20.wireOp",VERTEX,"E112.2.0.center");
            var Q28;
            Q28=sQuery(id+"F20.wireOp",VERTEX,"E114.center");
            var Q29;
            Q29=sQuery(id+"F20.wireOp",VERTEX,"E116.7.0.center");
            var Q30;
            Q30=sQuery(id+"F20.wireOp",VERTEX,"E116.6.0.center");
            var Q31;
            Q31=sQuery(id+"F20.wireOp",VERTEX,"E116.5.0.center");
            var Q32;
            Q32=sQuery(id+"F20.wireOp",VERTEX,"E116.4.0.center");
            var Q33;
            Q33=sQuery(id+"F20.wireOp",VERTEX,"E116.3.0.center");
            var Q34;
            Q34=sQuery(id+"F20.wireOp",VERTEX,"E116.2.0.center");
            var Q35;
            Q35=sQuery(id+"F20.wireOp",VERTEX,"E116.1.0.center");
            var Q36;
            Q36=sQuery(id+"F20.wireOp",VERTEX,"E120.3.0.center");
            var Q37;
            Q37=sQuery(id+"F20.wireOp",VERTEX,"E118.center");
            var Q38;
            Q38=sQuery(id+"F20.wireOp",VERTEX,"E120.2.0.center");
            var Q39;
            Q39=sQuery(id+"F20.wireOp",VERTEX,"E120.1.0.center");
            var Q40;
            Q40=sQuery(id+"F20.wireOp",VERTEX,"E122.center");
            var Q41;
            Q41=sQuery(id+"F20.wireOp",VERTEX,"E124.7.0.center");
            var Q42;
            Q42=sQuery(id+"F20.wireOp",VERTEX,"E124.6.0.center");
            var Q43;
            Q43=sQuery(id+"F20.wireOp",VERTEX,"E124.5.0.center");
            var Q44;
            Q44=sQuery(id+"F20.wireOp",VERTEX,"E124.4.0.center");
            var Q45;
            Q45=sQuery(id+"F20.wireOp",VERTEX,"E124.3.0.center");
            var Q46;
            Q46=sQuery(id+"F20.wireOp",VERTEX,"E124.2.0.center");
            var Q47;
            Q47=sQuery(id+"F20.wireOp",VERTEX,"E124.1.0.center");
            var Q48;
            Q48=makeQuery(id+"F18.opPattern","COPY",BODY,{"derivedFrom":makeQuery(id+"F12.opPattern","COPY",BODY,{"derivedFrom":makeQuery(id+"F6.opPattern","COPY",BODY,{"derivedFrom":makeQuery(id+"F1.opExtrude","SWEPT_BODY",BODY,{"disambiguationData":[OSD([sQuery(id+"F0.wireOp",EDGE,"E0"),sQuery(id+"F0.wireOp",EDGE,"E1"),sQuery(id+"F0.wireOp",EDGE,"E2"),sQuery(id+"F0.wireOp",EDGE,"E3.0"),sQuery(id+"F0.wireOp",EDGE,"E3.1"),sQuery(id+"F0.wireOp",EDGE,"E3.2"),sQuery(id+"F0.wireOp",EDGE,"E4"),sQuery(id+"F0.wireOp",EDGE,"E5")])]}),"instanceName":"1"}),"instanceName":"1"}),"instanceName":"1"});
            hole(context, id + "F23", {"style" : HoleStyle.SIMPLE, "holeDiameter" : 3.7 * mm, "endStyle" : HoleEndStyle.THROUGH, "locations" : qUnion([Q0, Q1, Q2, Q3, Q4, Q5, Q6, Q7, Q8, Q9, Q10, Q11, Q12, Q13, Q14, Q15, Q16, Q17, Q18, Q19, Q20, Q21, Q22, Q23, Q24, Q25, Q26, Q27, Q28, Q29, Q30, Q31, Q32, Q33, Q34, Q35, Q36, Q37, Q38, Q39, Q40, Q41, Q42, Q43, Q44, Q45, Q46, Q47]), "scope" : qUnion([Q48])});
        }
        {
            var Q0;
            Q0=makeQuery(id+"F18.opPattern","COPY",BODY,{"derivedFrom":makeQuery(id+"F12.opPattern","COPY",BODY,{"derivedFrom":makeQuery(id+"F6.opPattern","COPY",BODY,{"derivedFrom":makeQuery(id+"F1.opExtrude","SWEPT_BODY",BODY,{"disambiguationData":[OSD([sQuery(id+"F0.wireOp",EDGE,"E0"),sQuery(id+"F0.wireOp",EDGE,"E1"),sQuery(id+"F0.wireOp",EDGE,"E2"),sQuery(id+"F0.wireOp",EDGE,"E3.0"),sQuery(id+"F0.wireOp",EDGE,"E3.1"),sQuery(id+"F0.wireOp",EDGE,"E3.2"),sQuery(id+"F0.wireOp",EDGE,"E4"),sQuery(id+"F0.wireOp",EDGE,"E5")])]}),"instanceName":"1"}),"instanceName":"1"}),"instanceName":"1"});
            transform(context, id + "F24", {"entities" : qUnion([Q0]), "transformType" : TransformType.TRANSLATION_3D, "dx" : 86.13 * mm, "dy" : 0 * mm, "dz" : 0 * mm, "makeCopy" : true});
        }
        {
            var Q0;
            Q0=makeQuery(id+"F24.opPattern","COPY",FACE,{"derivedFrom":makeQuery(id+"F19.opExtrude","CAP_FACE",FACE,{"disambiguationData":[OSD([sQuery(id+"F0.wireOp",EDGE,"E0"),sQuery(id+"F0.wireOp",EDGE,"E1"),sQuery(id+"F0.wireOp",EDGE,"E2"),sQuery(id+"F0.wireOp",EDGE,"E3.0"),sQuery(id+"F0.wireOp",EDGE,"E3.1"),sQuery(id+"F0.wireOp",EDGE,"E3.2"),sQuery(id+"F0.wireOp",EDGE,"E4"),sQuery(id+"F0.wireOp",EDGE,"E5")])],"isStart":false}),"instanceName":"1"});
            extrude(context, id + "F25", {"entities" : qUnion([Q0]), "operationType" : NewBodyOperationType.ADD, "depth" : 128 * mm});
        }
        {
            var Q0;
            {var subQ0=sQuery(id+"F0.wireOp",EDGE,"E1");Q0=makeQuery(id+"F25.boolean.opBoolean","MERGE",FACE,{"derivedFrom":[makeQuery(id+"F24.opPattern","COPY",FACE,{"derivedFrom":makeQuery(id+"F19.boolean.opBoolean","MERGE",FACE,{"derivedFrom":[makeQuery(id+"F18.opPattern","COPY",FACE,{"derivedFrom":makeQuery(id+"F13.boolean.opBoolean","MERGE",FACE,{"derivedFrom":[makeQuery(id+"F12.opPattern","COPY",FACE,{"derivedFrom":makeQuery(id+"F7.boolean.opBoolean","MERGE",FACE,{"derivedFrom":[makeQuery(id+"F6.opPattern","COPY",FACE,{"derivedFrom":makeQuery(id+"F1.opExtrude","SWEPT_FACE",FACE,{"disambiguationData":[OSD([subQ0])]}),"instanceName":"1"}),makeQuery(id+"F7.opExtrude","SWEPT_FACE",FACE,{"disambiguationData":[OSD([subQ0])]})]}),"instanceName":"1"}),makeQuery(id+"F13.opExtrude","SWEPT_FACE",FACE,{"disambiguationData":[OSD([subQ0])]})]}),"instanceName":"1"}),makeQuery(id+"F19.opExtrude","SWEPT_FACE",FACE,{"disambiguationData":[OSD([subQ0])]})]}),"instanceName":"1"}),makeQuery(id+"F25.opExtrude","SWEPT_FACE",FACE,{"disambiguationData":[OSD([subQ0])]})]});}
            var sketch = newSketch(context, id + "F26", { "sketchPlane" : qUnion([Q0])});
            skPoint(sketch, "E143.center", {"position": v(368, -16) * mm});
            skPoint(sketch, "E144.center", {"position": v(400, -16) * mm});
            skCircle(sketch, "E145", {"center": v(320, -16) * mm, "radius": 4 * mm});
            skPoint(sketch, "E146.center", {"position": v(304, -16) * mm});
            skCircle(sketch, "E147", {"center": v(384, -16) * mm, "radius": 4 * mm});
            skPoint(sketch, "E148.center", {"position": v(336, -16) * mm});
            skCircle(sketch, "E143.3.0", {"center": v(368, -8) * mm, "radius": 1.85 * mm});
            skCircle(sketch, "E149", {"center": v(392, -16) * mm, "radius": 1.85 * mm});
            skCircle(sketch, "E144.1.0", {"center": v(394.34, -21.66) * mm, "radius": 1.85 * mm});
            skCircle(sketch, "E144.7.0", {"center": v(394.34, -10.34) * mm, "radius": 1.85 * mm});
            skCircle(sketch, "E150", {"center": v(360, -16) * mm, "radius": 1.85 * mm});
            skCircle(sketch, "E151", {"center": v(352, -16) * mm, "radius": 4 * mm});
            skCircle(sketch, "E144.5.0", {"center": v(405.66, -10.34) * mm, "radius": 1.85 * mm});
            skCircle(sketch, "E152", {"center": v(288, -16) * mm, "radius": 4 * mm});
            skCircle(sketch, "E153", {"center": v(296, -16) * mm, "radius": 1.85 * mm});
            skCircle(sketch, "E143.2.0", {"center": v(376, -16) * mm, "radius": 1.85 * mm});
            skCircle(sketch, "E154", {"center": v(400, -16) * mm, "radius": 4 * mm});
            skCircle(sketch, "E148.3.0", {"center": v(341.66, -21.66) * mm, "radius": 1.85 * mm});
            skCircle(sketch, "E146.2.0", {"center": v(312, -16) * mm, "radius": 1.85 * mm});
            skCircle(sketch, "E146.1.0", {"center": v(304, -24) * mm, "radius": 1.85 * mm});
            skCircle(sketch, "E146.3.0", {"center": v(304, -8) * mm, "radius": 1.85 * mm});
            skCircle(sketch, "E155", {"center": v(336, -16) * mm, "radius": 4 * mm});
            skCircle(sketch, "E156", {"center": v(328, -16) * mm, "radius": 1.85 * mm});
            skCircle(sketch, "E148.5.0", {"center": v(341.66, -10.34) * mm, "radius": 1.85 * mm});
            skCircle(sketch, "E148.4.0", {"center": v(344, -16) * mm, "radius": 1.85 * mm});
            skLineSegment(sketch, "E157", {"start": v(280, -16) * mm, "end": v(424, -16) * mm, "construction": true});
            skCircle(sketch, "E158.0", {"center": v(280, -16) * mm, "radius": 1.85 * mm});
            skCircle(sketch, "E159", {"center": v(304, -16) * mm, "radius": 4 * mm});
            skCircle(sketch, "E148.2.0", {"center": v(336, -24) * mm, "radius": 1.85 * mm});
            skCircle(sketch, "E148.1.0", {"center": v(330.34, -21.66) * mm, "radius": 1.85 * mm});
            skCircle(sketch, "E144.4.0", {"center": v(408, -16) * mm, "radius": 1.85 * mm});
            skCircle(sketch, "E144.3.0", {"center": v(405.66, -21.66) * mm, "radius": 1.85 * mm});
            skCircle(sketch, "E160", {"center": v(368, -16) * mm, "radius": 4 * mm});
            skCircle(sketch, "E144.2.0", {"center": v(400, -24) * mm, "radius": 1.85 * mm});
            skCircle(sketch, "E144.6.0", {"center": v(400, -8) * mm, "radius": 1.85 * mm});
            skCircle(sketch, "E148.6.0", {"center": v(336, -8) * mm, "radius": 1.85 * mm});
            skCircle(sketch, "E143.1.0", {"center": v(368, -24) * mm, "radius": 1.85 * mm});
            skCircle(sketch, "E148.7.0", {"center": v(330.34, -10.34) * mm, "radius": 1.85 * mm});
            skSolve(sketch);
        }
        {
            var Q0;
            {var subQ0=sQuery(id+"F0.wireOp",EDGE,"E0");Q0=makeQuery(id+"F25.boolean.opBoolean","MERGE",FACE,{"derivedFrom":[makeQuery(id+"F24.opPattern","COPY",FACE,{"derivedFrom":makeQuery(id+"F19.boolean.opBoolean","MERGE",FACE,{"derivedFrom":[makeQuery(id+"F18.opPattern","COPY",FACE,{"derivedFrom":makeQuery(id+"F13.boolean.opBoolean","MERGE",FACE,{"derivedFrom":[makeQuery(id+"F12.opPattern","COPY",FACE,{"derivedFrom":makeQuery(id+"F7.boolean.opBoolean","MERGE",FACE,{"derivedFrom":[makeQuery(id+"F6.opPattern","COPY",FACE,{"derivedFrom":makeQuery(id+"F1.opExtrude","SWEPT_FACE",FACE,{"disambiguationData":[OSD([subQ0])]}),"instanceName":"1"}),makeQuery(id+"F7.opExtrude","SWEPT_FACE",FACE,{"disambiguationData":[OSD([subQ0])]})]}),"instanceName":"1"}),makeQuery(id+"F13.opExtrude","SWEPT_FACE",FACE,{"disambiguationData":[OSD([subQ0])]})]}),"instanceName":"1"}),makeQuery(id+"F19.opExtrude","SWEPT_FACE",FACE,{"disambiguationData":[OSD([subQ0])]})]}),"instanceName":"1"}),makeQuery(id+"F25.opExtrude","SWEPT_FACE",FACE,{"disambiguationData":[OSD([subQ0])]})]});}
            var sketch = newSketch(context, id + "F27", { "sketchPlane" : qUnion([Q0])});
            skPoint(sketch, "E161.center", {"position": v(344.5, 336) * mm});
            skPoint(sketch, "E162.center", {"position": v(344.5, 400) * mm});
            skPoint(sketch, "E163.center", {"position": v(344.5, 304) * mm});
            skPoint(sketch, "E164.center", {"position": v(344.5, 368) * mm});
            skCircle(sketch, "E161.5.0", {"center": v(338.85, 341.66) * mm, "radius": 1.85 * mm});
            skCircle(sketch, "E161.6.0", {"center": v(336.5, 336) * mm, "radius": 1.85 * mm});
            skCircle(sketch, "E165", {"center": v(344.5, 352) * mm, "radius": 4 * mm});
            skCircle(sketch, "E161.7.0", {"center": v(338.85, 330.34) * mm, "radius": 1.85 * mm});
            skCircle(sketch, "E161.3.0", {"center": v(350.16, 341.66) * mm, "radius": 1.85 * mm});
            skCircle(sketch, "E166", {"center": v(344.5, 288) * mm, "radius": 4 * mm});
            skLineSegment(sketch, "E167", {"start": v(344.5, 280) * mm, "end": v(344.5, 416) * mm});
            skCircle(sketch, "E168", {"center": v(344.5, 336) * mm, "radius": 4 * mm});
            skCircle(sketch, "E162.6.0", {"center": v(336.5, 400) * mm, "radius": 1.85 * mm});
            skCircle(sketch, "E162.7.0", {"center": v(338.85, 394.34) * mm, "radius": 1.85 * mm});
            skCircle(sketch, "E169", {"center": v(344.5, 368) * mm, "radius": 4 * mm});
            skCircle(sketch, "E170", {"center": v(344.5, 360) * mm, "radius": 1.85 * mm});
            skCircle(sketch, "E161.4.0", {"center": v(344.5, 344) * mm, "radius": 1.85 * mm});
            skCircle(sketch, "E161.1.0", {"center": v(350.16, 330.34) * mm, "radius": 1.85 * mm});
            skCircle(sketch, "E162.3.0", {"center": v(350.16, 405.66) * mm, "radius": 1.85 * mm});
            skCircle(sketch, "E162.5.0", {"center": v(338.85, 405.66) * mm, "radius": 1.85 * mm});
            skCircle(sketch, "E162.2.0", {"center": v(352.5, 400) * mm, "radius": 1.85 * mm});
            skCircle(sketch, "E171", {"center": v(344.5, 320) * mm, "radius": 4 * mm});
            skCircle(sketch, "E172", {"center": v(344.5, 328) * mm, "radius": 1.85 * mm});
            skCircle(sketch, "E164.3.0", {"center": v(336.5, 368) * mm, "radius": 1.85 * mm});
            skCircle(sketch, "E173", {"center": v(344.5, 400) * mm, "radius": 4 * mm});
            skCircle(sketch, "E162.4.0", {"center": v(344.5, 408) * mm, "radius": 1.85 * mm});
            skCircle(sketch, "E164.2.0", {"center": v(344.5, 376) * mm, "radius": 1.85 * mm});
            skCircle(sketch, "E164.1.0", {"center": v(352.5, 368) * mm, "radius": 1.85 * mm});
            skCircle(sketch, "E174", {"center": v(344.5, 392) * mm, "radius": 1.85 * mm});
            skCircle(sketch, "E175", {"center": v(344.5, 384) * mm, "radius": 4 * mm});
            skCircle(sketch, "E162.1.0", {"center": v(350.16, 394.34) * mm, "radius": 1.85 * mm});
            skCircle(sketch, "E161.2.0", {"center": v(352.5, 336) * mm, "radius": 1.85 * mm});
            skCircle(sketch, "E163.1.0", {"center": v(352.5, 304) * mm, "radius": 1.85 * mm});
            skCircle(sketch, "E176", {"center": v(344.5, 304) * mm, "radius": 4 * mm});
            skCircle(sketch, "E177", {"center": v(344.5, 296) * mm, "radius": 1.85 * mm});
            skCircle(sketch, "E163.2.0", {"center": v(344.5, 312) * mm, "radius": 1.85 * mm});
            skCircle(sketch, "E163.3.0", {"center": v(336.5, 304) * mm, "radius": 1.85 * mm});
            skCircle(sketch, "E178.0", {"center": v(344.5, 280) * mm, "radius": 1.85 * mm});
            skSolve(sketch);
        }
        {
            var Q0;
            Q0=sQuery(id+"F26.wireOp",VERTEX,"E152.center");
            var Q1;
            Q1=sQuery(id+"F27.wireOp",VERTEX,"E166.center");
            var Q2;
            Q2=sQuery(id+"F27.wireOp",VERTEX,"E163.center");
            var Q3;
            Q3=sQuery(id+"F26.wireOp",VERTEX,"E146.center");
            var Q4;
            Q4=sQuery(id+"F27.wireOp",VERTEX,"E171.center");
            var Q5;
            Q5=sQuery(id+"F26.wireOp",VERTEX,"E145.center");
            var Q6;
            Q6=sQuery(id+"F27.wireOp",VERTEX,"E161.center");
            var Q7;
            Q7=sQuery(id+"F26.wireOp",VERTEX,"E148.center");
            var Q8;
            Q8=sQuery(id+"F27.wireOp",VERTEX,"E165.center");
            var Q9;
            Q9=sQuery(id+"F26.wireOp",VERTEX,"E151.center");
            var Q10;
            Q10=sQuery(id+"F27.wireOp",VERTEX,"E164.center");
            var Q11;
            Q11=sQuery(id+"F26.wireOp",VERTEX,"E143.center");
            var Q12;
            Q12=sQuery(id+"F27.wireOp",VERTEX,"E175.center");
            var Q13;
            Q13=sQuery(id+"F26.wireOp",VERTEX,"E147.center");
            var Q14;
            Q14=sQuery(id+"F27.wireOp",VERTEX,"E162.center");
            var Q15;
            Q15=sQuery(id+"F26.wireOp",VERTEX,"E144.center");
            var Q16;
            Q16=makeQuery(id+"F24.opPattern","COPY",BODY,{"derivedFrom":makeQuery(id+"F18.opPattern","COPY",BODY,{"derivedFrom":makeQuery(id+"F12.opPattern","COPY",BODY,{"derivedFrom":makeQuery(id+"F6.opPattern","COPY",BODY,{"derivedFrom":makeQuery(id+"F1.opExtrude","SWEPT_BODY",BODY,{"disambiguationData":[OSD([sQuery(id+"F0.wireOp",EDGE,"E0"),sQuery(id+"F0.wireOp",EDGE,"E1"),sQuery(id+"F0.wireOp",EDGE,"E2"),sQuery(id+"F0.wireOp",EDGE,"E3.0"),sQuery(id+"F0.wireOp",EDGE,"E3.1"),sQuery(id+"F0.wireOp",EDGE,"E3.2"),sQuery(id+"F0.wireOp",EDGE,"E4"),sQuery(id+"F0.wireOp",EDGE,"E5")])]}),"instanceName":"1"}),"instanceName":"1"}),"instanceName":"1"}),"instanceName":"1"});
            hole(context, id + "F28", {"style" : HoleStyle.SIMPLE, "holeDiameter" : 8 * mm, "endStyle" : HoleEndStyle.THROUGH, "locations" : qUnion([Q0, Q1, Q2, Q3, Q4, Q5, Q6, Q7, Q8, Q9, Q10, Q11, Q12, Q13, Q14, Q15]), "scope" : qUnion([Q16])});
        }
        {
            var Q0;
            Q0=sQuery(id+"F27.wireOp",VERTEX,"E177.center");
            var Q1;
            Q1=sQuery(id+"F26.wireOp",VERTEX,"E153.center");
            var Q2;
            Q2=sQuery(id+"F27.wireOp",VERTEX,"E163.1.0.center");
            var Q3;
            Q3=sQuery(id+"F27.wireOp",VERTEX,"E163.3.0.center");
            var Q4;
            Q4=sQuery(id+"F26.wireOp",VERTEX,"E146.3.0.center");
            var Q5;
            Q5=sQuery(id+"F26.wireOp",VERTEX,"E146.1.0.center");
            var Q6;
            Q6=sQuery(id+"F26.wireOp",VERTEX,"E146.2.0.center");
            var Q7;
            Q7=sQuery(id+"F27.wireOp",VERTEX,"E163.2.0.center");
            var Q8;
            Q8=sQuery(id+"F27.wireOp",VERTEX,"E172.center");
            var Q9;
            Q9=sQuery(id+"F26.wireOp",VERTEX,"E156.center");
            var Q10;
            Q10=sQuery(id+"F26.wireOp",VERTEX,"E148.7.0.center");
            var Q11;
            Q11=sQuery(id+"F27.wireOp",VERTEX,"E161.7.0.center");
            var Q12;
            Q12=sQuery(id+"F27.wireOp",VERTEX,"E161.1.0.center");
            var Q13;
            Q13=sQuery(id+"F26.wireOp",VERTEX,"E148.1.0.center");
            var Q14;
            Q14=sQuery(id+"F26.wireOp",VERTEX,"E148.2.0.center");
            var Q15;
            Q15=sQuery(id+"F26.wireOp",VERTEX,"E148.6.0.center");
            var Q16;
            Q16=sQuery(id+"F27.wireOp",VERTEX,"E161.2.0.center");
            var Q17;
            Q17=sQuery(id+"F27.wireOp",VERTEX,"E161.6.0.center");
            var Q18;
            Q18=sQuery(id+"F27.wireOp",VERTEX,"E161.3.0.center");
            var Q19;
            Q19=sQuery(id+"F27.wireOp",VERTEX,"E161.5.0.center");
            var Q20;
            Q20=sQuery(id+"F26.wireOp",VERTEX,"E148.5.0.center");
            var Q21;
            Q21=sQuery(id+"F26.wireOp",VERTEX,"E148.3.0.center");
            var Q22;
            Q22=sQuery(id+"F26.wireOp",VERTEX,"E148.4.0.center");
            var Q23;
            Q23=sQuery(id+"F27.wireOp",VERTEX,"E161.4.0.center");
            var Q24;
            Q24=sQuery(id+"F26.wireOp",VERTEX,"E150.center");
            var Q25;
            Q25=sQuery(id+"F27.wireOp",VERTEX,"E170.center");
            var Q26;
            Q26=sQuery(id+"F27.wireOp",VERTEX,"E164.1.0.center");
            var Q27;
            Q27=sQuery(id+"F27.wireOp",VERTEX,"E164.3.0.center");
            var Q28;
            Q28=sQuery(id+"F26.wireOp",VERTEX,"E143.3.0.center");
            var Q29;
            Q29=sQuery(id+"F26.wireOp",VERTEX,"E143.1.0.center");
            var Q30;
            Q30=sQuery(id+"F26.wireOp",VERTEX,"E143.2.0.center");
            var Q31;
            Q31=sQuery(id+"F27.wireOp",VERTEX,"E164.2.0.center");
            var Q32;
            Q32=sQuery(id+"F27.wireOp",VERTEX,"E174.center");
            var Q33;
            Q33=sQuery(id+"F27.wireOp",VERTEX,"E162.7.0.center");
            var Q34;
            Q34=sQuery(id+"F27.wireOp",VERTEX,"E162.1.0.center");
            var Q35;
            Q35=sQuery(id+"F26.wireOp",VERTEX,"E149.center");
            var Q36;
            Q36=sQuery(id+"F26.wireOp",VERTEX,"E144.7.0.center");
            var Q37;
            Q37=sQuery(id+"F26.wireOp",VERTEX,"E144.1.0.center");
            var Q38;
            Q38=sQuery(id+"F26.wireOp",VERTEX,"E144.6.0.center");
            var Q39;
            Q39=sQuery(id+"F26.wireOp",VERTEX,"E144.2.0.center");
            var Q40;
            Q40=sQuery(id+"F26.wireOp",VERTEX,"E144.5.0.center");
            var Q41;
            Q41=sQuery(id+"F26.wireOp",VERTEX,"E144.3.0.center");
            var Q42;
            Q42=sQuery(id+"F26.wireOp",VERTEX,"E144.4.0.center");
            var Q43;
            Q43=sQuery(id+"F27.wireOp",VERTEX,"E162.2.0.center");
            var Q44;
            Q44=sQuery(id+"F27.wireOp",VERTEX,"E162.6.0.center");
            var Q45;
            Q45=sQuery(id+"F27.wireOp",VERTEX,"E162.5.0.center");
            var Q46;
            Q46=sQuery(id+"F27.wireOp",VERTEX,"E162.4.0.center");
            var Q47;
            Q47=sQuery(id+"F27.wireOp",VERTEX,"E162.3.0.center");
            var Q48;
            Q48=makeQuery(id+"F24.opPattern","COPY",BODY,{"derivedFrom":makeQuery(id+"F18.opPattern","COPY",BODY,{"derivedFrom":makeQuery(id+"F12.opPattern","COPY",BODY,{"derivedFrom":makeQuery(id+"F6.opPattern","COPY",BODY,{"derivedFrom":makeQuery(id+"F1.opExtrude","SWEPT_BODY",BODY,{"disambiguationData":[OSD([sQuery(id+"F0.wireOp",EDGE,"E0"),sQuery(id+"F0.wireOp",EDGE,"E1"),sQuery(id+"F0.wireOp",EDGE,"E2"),sQuery(id+"F0.wireOp",EDGE,"E3.0"),sQuery(id+"F0.wireOp",EDGE,"E3.1"),sQuery(id+"F0.wireOp",EDGE,"E3.2"),sQuery(id+"F0.wireOp",EDGE,"E4"),sQuery(id+"F0.wireOp",EDGE,"E5")])]}),"instanceName":"1"}),"instanceName":"1"}),"instanceName":"1"}),"instanceName":"1"});
            hole(context, id + "F29", {"style" : HoleStyle.SIMPLE, "holeDiameter" : 3.7 * mm, "endStyle" : HoleEndStyle.THROUGH, "locations" : qUnion([Q0, Q1, Q2, Q3, Q4, Q5, Q6, Q7, Q8, Q9, Q10, Q11, Q12, Q13, Q14, Q15, Q16, Q17, Q18, Q19, Q20, Q21, Q22, Q23, Q24, Q25, Q26, Q27, Q28, Q29, Q30, Q31, Q32, Q33, Q34, Q35, Q36, Q37, Q38, Q39, Q40, Q41, Q42, Q43, Q44, Q45, Q46, Q47]), "scope" : qUnion([Q48])});
        }
    });
